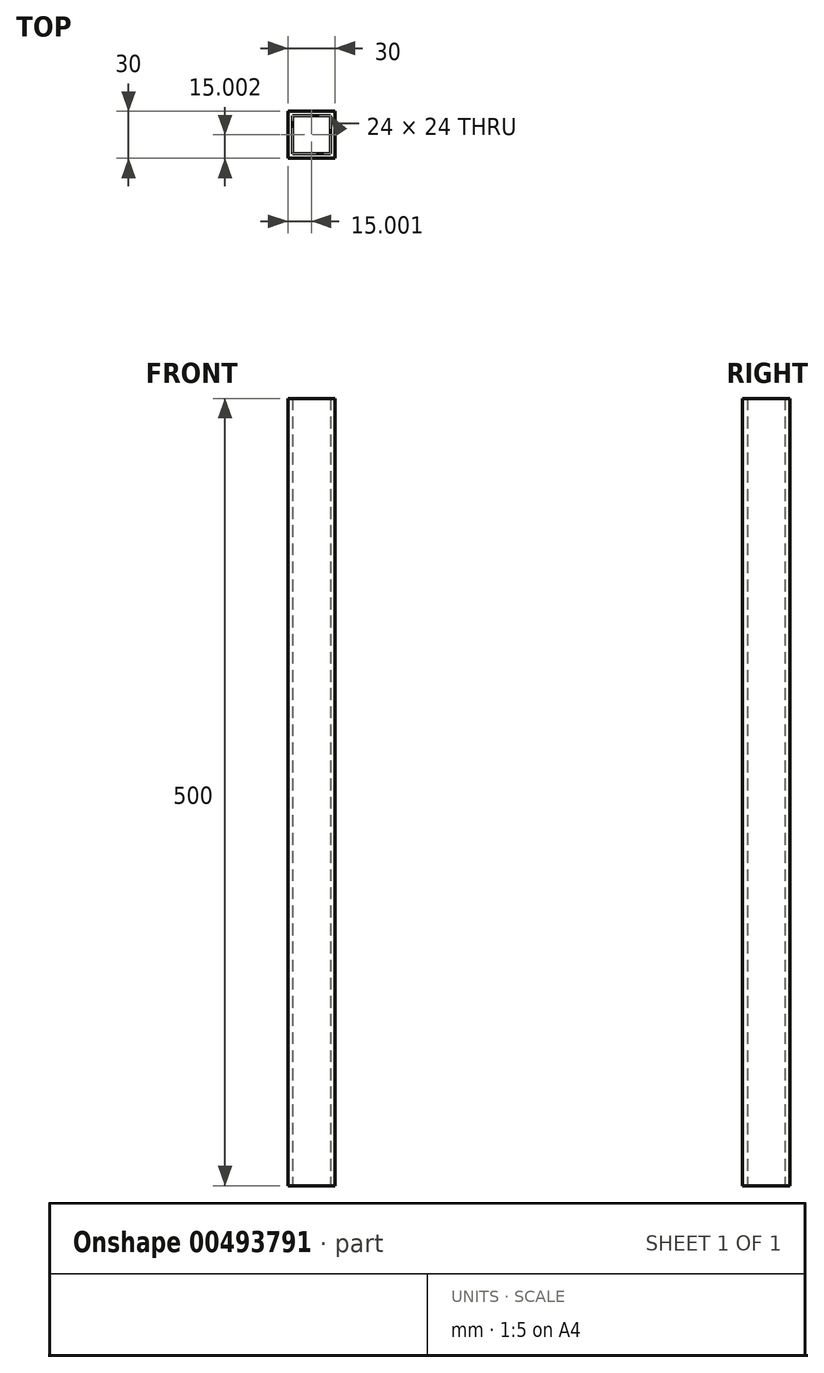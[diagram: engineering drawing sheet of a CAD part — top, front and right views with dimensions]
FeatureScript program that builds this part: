
annotation { "Feature Type Name" : "Feature", "Feature Type Description" : "" }
export const myFeature = defineFeature(function(context is Context, id is Id, definition is map)
    precondition{}
    {
        {
            var Q0;
            Q0=qCreatedBy(makeId("Top.planeOp"),FACE);
            var sketch = newSketch(context, id + "F0", { "sketchPlane" : qUnion([Q0])});
            skLineSegment(sketch, "E0.bottom", {"start": v(-12.6, 13.15) * mm, "end": v(11.4, 13.15) * mm});
            skLineSegment(sketch, "E0.top", {"start": v(-12.6, -10.85) * mm, "end": v(11.4, -10.85) * mm});
            skLineSegment(sketch, "E0.left", {"start": v(-12.6, 13.15) * mm, "end": v(-12.6, -10.85) * mm});
            skLineSegment(sketch, "E0.right", {"start": v(11.4, 13.15) * mm, "end": v(11.4, -10.85) * mm});
            skLineSegment(sketch, "E1.bottom", {"start": v(-15.6, 16.15) * mm, "end": v(14.4, 16.15) * mm});
            skLineSegment(sketch, "E1.top", {"start": v(-15.6, -13.85) * mm, "end": v(14.4, -13.85) * mm});
            skLineSegment(sketch, "E1.left", {"start": v(-15.6, 16.15) * mm, "end": v(-15.6, -13.85) * mm});
            skLineSegment(sketch, "E1.right", {"start": v(14.4, 16.15) * mm, "end": v(14.4, -13.85) * mm});
            skSolve(sketch);
        }
        {
            var Q0;
            Q0 = qSketchRegion(id + "F0", true);
            extrude(context, id + "F1", {"entities" : qUnion([Q0]), "depth" : 500 * mm});
        }
    });
